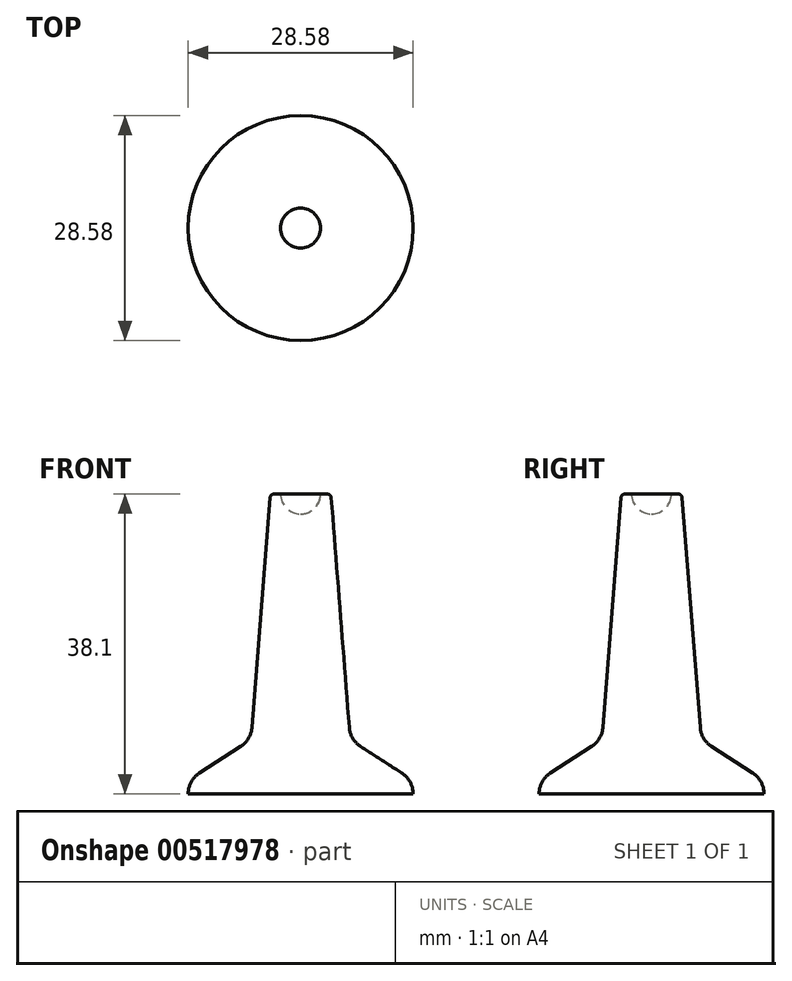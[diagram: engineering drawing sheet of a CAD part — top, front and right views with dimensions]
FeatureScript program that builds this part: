
annotation { "Feature Type Name" : "Feature", "Feature Type Description" : "" }
export const myFeature = defineFeature(function(context is Context, id is Id, definition is map)
    precondition{}
    {
        {
            var Q0;
            Q0=qCreatedBy(makeId("Front.planeOp"),FACE);
            var sketch = newSketch(context, id + "F0", { "sketchPlane" : qUnion([Q0])});
            skLineSegment(sketch, "E0", {"start": v(0, 38.1) * mm, "end": v(0, 0) * mm});
            skLineSegment(sketch, "E1", {"start": v(0, 0) * mm, "end": v(14.29, 0) * mm});
            skLineSegment(sketch, "E2", {"start": v(2.54, 38.1) * mm, "end": v(3.38, 38.1) * mm});
            skLineSegment(sketch, "E3", {"start": v(3.88, 37.63) * mm, "end": v(6.18, 8.43) * mm});
            skArc(sketch, "E4", {"start": v(14.29, 0) * mm, "mid": v(13.9, 1.52) * mm, "end": v(12.83, 2.67) * mm});
            skArc(sketch, "E5", {"start": v(6.18, 8.43) * mm, "mid": v(6.62, 7.05) * mm, "end": v(7.63, 6.01) * mm});
            skLineSegment(sketch, "E6", {"start": v(7.63, 6.01) * mm, "end": v(12.83, 2.67) * mm});
            skPoint(sketch, "E7.visualSharp", {"position": v(3.85, 38.1) * mm});
            skArc(sketch, "E7.filletArc", {"start": v(3.88, 37.63) * mm, "mid": v(3.72, 37.97) * mm, "end": v(3.38, 38.1) * mm});
            skArc(sketch, "E8", {"start": v(0, 35.56) * mm, "mid": v(1.8, 36.3) * mm, "end": v(2.54, 38.1) * mm});
            skSolve(sketch);
        }
        {
            var Q0;
            Q0 = qSketchRegion(id + "F0", true);
            var Q1;
            Q1=sQuery(id+"F0.wireOp",EDGE,"E0");
            revolve(context, id + "F1", {"entities" : qUnion([Q0]), "axis" : qUnion([Q1]), "revolveType" : RevolveType.FULL});
        }
    });
